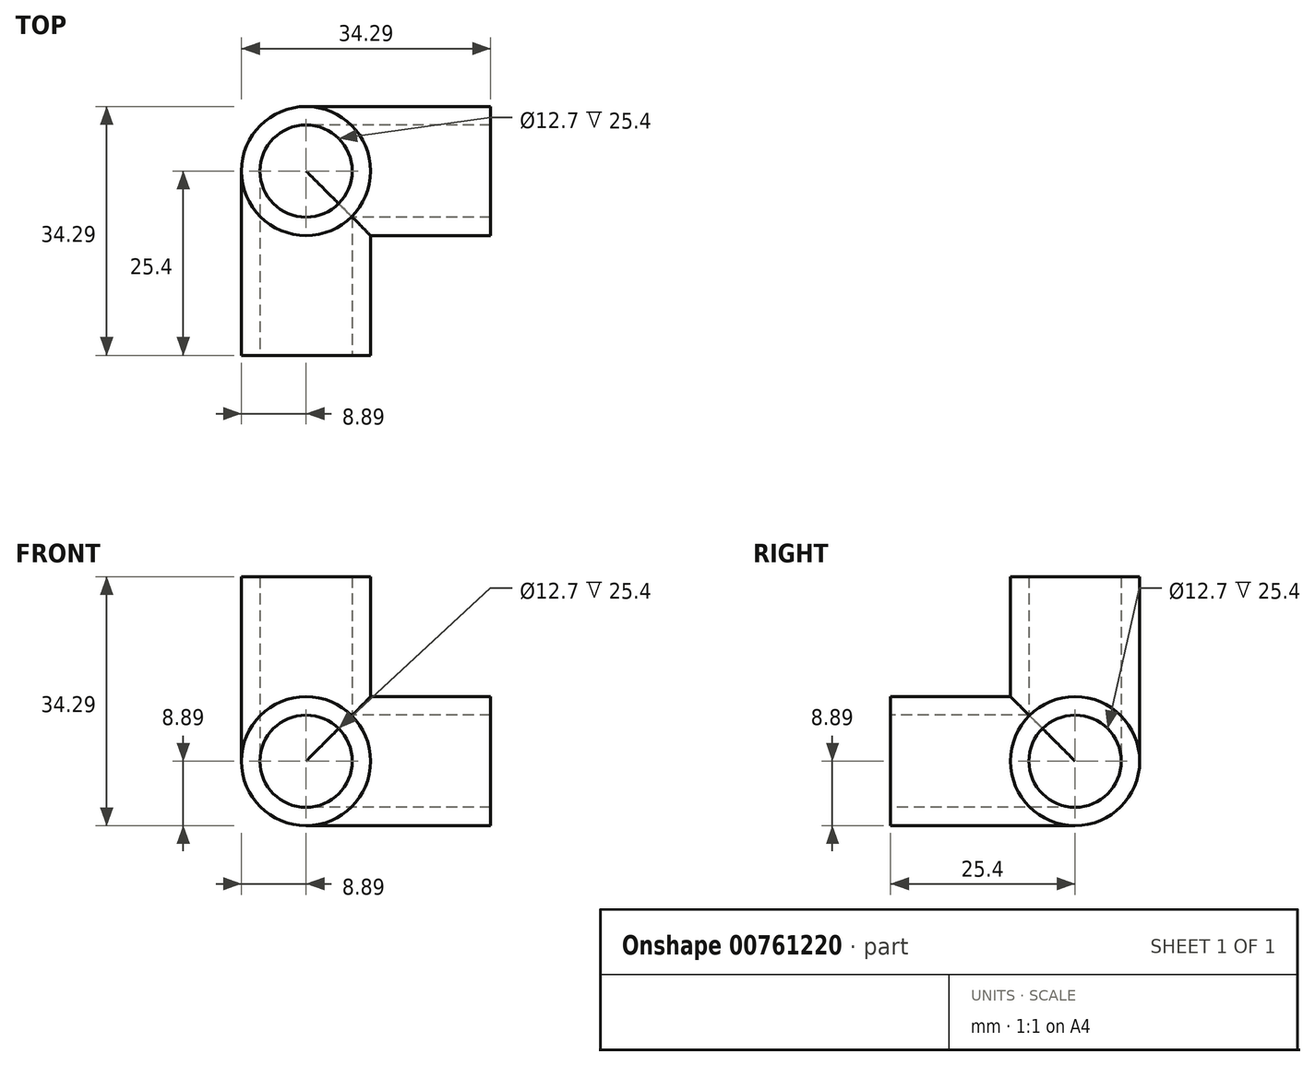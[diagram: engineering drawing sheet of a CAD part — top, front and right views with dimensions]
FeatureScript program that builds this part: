
annotation { "Feature Type Name" : "Feature", "Feature Type Description" : "" }
export const myFeature = defineFeature(function(context is Context, id is Id, definition is map)
    precondition{}
    {
        {
            var Q0;
            Q0=qCreatedBy(makeId("Top.planeOp"),FACE);
            var sketch = newSketch(context, id + "F0", { "sketchPlane" : qUnion([Q0])});
            skCircle(sketch, "E0", {"center": v(0, 0) * mm, "radius": 8.9 * mm});
            skLineSegment(sketch, "E1", {"start": v(0, 8.9) * mm, "end": v(0, 0) * mm});
            skLineSegment(sketch, "E2", {"start": v(0, 0) * mm, "end": v(25.4, 0) * mm});
            skLineSegment(sketch, "E3", {"start": v(25.4, 0) * mm, "end": v(25.4, 8.9) * mm});
            skLineSegment(sketch, "E4", {"start": v(25.4, 8.9) * mm, "end": v(0, 8.9) * mm});
            skLineSegment(sketch, "E5", {"start": v(-8.9, 0) * mm, "end": v(-8.89, -25.4) * mm});
            skLineSegment(sketch, "E6", {"start": v(-8.89, -25.4) * mm, "end": v(0, -25.4) * mm});
            skLineSegment(sketch, "E7", {"start": v(0, -25.4) * mm, "end": v(0, 0) * mm});
            skLineSegment(sketch, "E8", {"start": v(-8.9, 0) * mm, "end": v(0, 0) * mm});
            skSolve(sketch);
        }
        {
            var Q0;
            {var subQ0=sQuery(id+"F0.wireOp",EDGE,"E1");Q0=makeQuery(id+"F0.imprint","IMPRINT",FACE,{"disambiguationData":[TD([[makeQuery(id+"F0.imprint","IMPRINT",EDGE,{"derivedFrom":subQ0}),-1.0]])]});}
            var Q1;
            {var subQ0=sQuery(id+"F0.wireOp",EDGE,"E8");Q1=makeQuery(id+"F0.imprint","IMPRINT",FACE,{"disambiguationData":[TD([[makeQuery(id+"F0.imprint","IMPRINT",EDGE,{"derivedFrom":subQ0}),-1.0]])]});}
            var Q2;
            {var subQ0=sQuery(id+"F0.wireOp",EDGE,"E2");var subQ1=sQuery(id+"F0.wireOp",EDGE,"E0");var subQ2=makeQuery(id+"F0.imprint","INTERSECT",VERTEX,{"derivedFrom":[subQ1,subQ0]});Q2=makeQuery(id+"F0.imprint","IMPRINT",FACE,{"disambiguationData":[TD([[makeQuery(id+"F0.imprint","IMPRINT",EDGE,{"disambiguationData":[TD([[subQ2,1.0]])],"derivedFrom":subQ1}),1.0]])]});}
            var Q3;
            {var subQ0=sQuery(id+"F0.wireOp",EDGE,"E1");Q3=makeQuery(id+"F0.imprint","IMPRINT",FACE,{"disambiguationData":[TD([[makeQuery(id+"F0.imprint","IMPRINT",EDGE,{"derivedFrom":subQ0}),1.0]])]});}
            extrude(context, id + "F1", {"entities" : qUnion([Q0, Q1, Q2, Q3]), "flatOperationType" : FlatOperationType.REMOVE, "depth" : 25.4 * mm, "offsetDistance" : 25.4 * mm, "domain" : OperationDomain.MODEL});
        }
        {
            var Q0;
            {var subQ0=sQuery(id+"F0.wireOp",EDGE,"E1");Q0=makeQuery(id+"F0.imprint","IMPRINT",FACE,{"disambiguationData":[TD([[makeQuery(id+"F0.imprint","IMPRINT",EDGE,{"derivedFrom":subQ0}),1.0]])]});}
            var Q1;
            {var subQ4=sQuery(id+"F0.wireOp",EDGE,"E3");Q1=makeQuery(id+"F0.imprint","IMPRINT",FACE,{"disambiguationData":[TD([[makeQuery(id+"F0.imprint","IMPRINT",EDGE,{"derivedFrom":subQ4}),1.0]])]});}
            var Q2;
            Q2=sQuery(id+"F0.wireOp",EDGE,"E2");
            revolve(context, id + "F2", {"operationType" : NewBodyOperationType.ADD, "surfaceOperationType" : NewSurfaceOperationType.NEW, "entities" : qUnion([Q0, Q1]), "axis" : qUnion([Q2]), "revolveType" : RevolveType.FULL});
        }
        {
            var Q0;
            {var subQ0=sQuery(id+"F0.wireOp",EDGE,"E8");Q0=makeQuery(id+"F0.imprint","IMPRINT",FACE,{"disambiguationData":[TD([[makeQuery(id+"F0.imprint","IMPRINT",EDGE,{"derivedFrom":subQ0}),-1.0]])]});}
            var Q1;
            {var subQ0=sQuery(id+"F0.wireOp",EDGE,"E5");Q1=makeQuery(id+"F0.imprint","IMPRINT",FACE,{"disambiguationData":[TD([[makeQuery(id+"F0.imprint","IMPRINT",EDGE,{"derivedFrom":subQ0}),1.0]])]});}
            var Q2;
            Q2=sQuery(id+"F0.wireOp",EDGE,"E7");
            revolve(context, id + "F3", {"operationType" : NewBodyOperationType.ADD, "surfaceOperationType" : NewSurfaceOperationType.NEW, "entities" : qUnion([Q0, Q1]), "axis" : qUnion([Q2]), "revolveType" : RevolveType.FULL});
        }
        {
            var Q0;
            Q0=makeQuery(id+"F2.opRevolve","SWEPT_FACE",FACE,{"disambiguationData":[OSD([sQuery(id+"F0.wireOp",EDGE,"E1")])]});
            cPlane(context, id + "F4", {"entities" : qUnion([Q0]), "cplaneType" : CPlaneType.OFFSET, "offset" : 6.35 * mm, "width" : 152.4 * mm, "height" : 152.4 * mm});
        }
        {
            var Q0;
            Q0=qCreatedBy(id+"F4.planeOp",FACE);
            var sketch = newSketch(context, id + "F5", { "sketchPlane" : qUnion([Q0])});
            skArc(sketch, "E9", {"start": v(-6.35, 0) * mm, "mid": v(-4.5, -4.5) * mm, "end": v(0, -6.35) * mm});
            skSolve(sketch);
        }
        {
            var Q0;
            {var subQ0=sQuery(id+"F0.wireOp",EDGE,"E1");Q0=makeQuery(id+"F0.imprint","IMPRINT",FACE,{"disambiguationData":[TD([[makeQuery(id+"F0.imprint","IMPRINT",EDGE,{"derivedFrom":subQ0}),-1.0]])]});}
            var Q1;
            Q1=sQuery(id+"F5.wireOp",EDGE,"E9");
            sweep(context, id + "F6", {"operationType" : NewBodyOperationType.ADD, "profiles" : qUnion([Q0]), "path" : qUnion([Q1])});
        }
        {
            var Q0;
            Q0=makeQuery(id+"F3.opRevolve","SWEPT_FACE",FACE,{"disambiguationData":[OSD([sQuery(id+"F0.wireOp",EDGE,"E6")])]});
            var Q1;
            Q1=makeQuery(id+"F1.opExtrude","CAP_FACE",FACE,{"disambiguationData":[OSD([sQuery(id+"F0.wireOp",EDGE,"E0")])],"isStart":false});
            var Q2;
            Q2=makeQuery(id+"F2.opRevolve","SWEPT_FACE",FACE,{"disambiguationData":[OSD([sQuery(id+"F0.wireOp",EDGE,"E3")])]});
            var Q3;
            Q3=makeQuery(id+"F1.opExtrude","SWEPT_BODY",BODY,{"disambiguationData":[OSD([sQuery(id+"F0.wireOp",EDGE,"E0")])]});
            shell(context, id + "F7", {"entities" : qUnion([Q0, Q1, Q2]), "parts" : qUnion([Q3]), "thickness" : 2.54 * mm});
        }
    });
